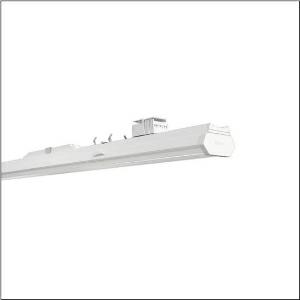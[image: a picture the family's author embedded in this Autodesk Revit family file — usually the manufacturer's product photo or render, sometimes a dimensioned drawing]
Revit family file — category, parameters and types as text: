
# Revit family: licross_r__11_protected_ho_51tp12dn4exl3s_b7b1
name_source: partatom
category: Lighting Fixtures
units: mm (PartAtom-declared; Revit-internal decimal feet)

## family parameters
Cut with Voids When Loaded = No
Host = Face
Light Source = No
Part Type = Normal
Room Calculation Point = No
Round Connector Dimension = Use Diameter
Shared = No

## types (1)
- --- (1 x LED, 850 lm, 5 W, 4000K)
    Apparent Load = 5 VA
    CIE Flux Codes = 70 91 97 98 100
    Color Rendering = 80
    Color Temperature = 4000K
    Default Elevation = 1800 mm
    Description = Licross® 11 Protected HO, luminaire insert, of sheet steel, galvanised, coil coated, white, length: 1.500mm, width: 90mm, height: 101mm, LED rated luminous flux: 14.070lm, light colour: 840, control gear: DALI 2, control gear: ECG DALI, with plug, 6-pole, with phase selection, for trunking rail, 14-core, mains connection: 220..240V, AC/DC, 0/50..60Hz, halogen-free wiring, for emergency light function, converter,control gear: single battery element, battery: LiFeP04, 9Ah, primary optical cover: cover, of PMMA, light emission: direct with ceiling illumination distribution, protection rating (complete): IP64, insulation class (complete): insulation class I (protective earthing), certification: CE, UKCA, protection symbol: D if used in an environment with conductive dust loads with corresponding accessories, permissible ambient temperature for indoor applications: +5..+30°C, standard: EN 60598-2-22, corresponds to IFS (International Featured Standards) requirements for safety and quality in the food industry, reducing of maximum allowable ambient temperature of 5°C with ceiling mounting, LABS conformity tested according to VDMA 24364:2018-05, packaging unit: 1 piece
    Height = 92 mm
    Lamp = 1 x LED
    Lamp Light Flux = 850 lm
    Lamp Power = 5 W
    Lamp count = 1
    Length = 1500 mm
    Luminous efficacy = 170 lm/W
    Manufacturer = Siteco
    ModVariant = No
    Model = 51TP12DN4EXL3S
    Mounting Place = Ceiling
    Mounting Type = Pendant
    Number of Poles = 1
    OnlyDefault = Yes
    Power Factor = 1
    Product Name = Licross® 11 Protected HO
    Product group = luminaire insert
    ProductGroupID = 902
    Protection Class = Protection class I
    Protection Degree = IP 64
    RLX_Detail_Level = 1
    RlxData = <blob elided: 24881 chars, md5=e11d46b7>
    Socket = socket
    Standby Power = 0 W
    System Light Flux = 850 lm
    System Power = 5 W
    Type Comments = : emergency light operation: 3 h
    Type Image = l_1256148.jpg
    URL = http://relux.com
    VarID = @adj_126123
    Voltage = 0 V
    Weight = 0.00 kg
    Width = 88 mm

## geometry (parser evidence)
native form markers: Blend x4, Sweep x12
no freeform markers — native parametric forms only
